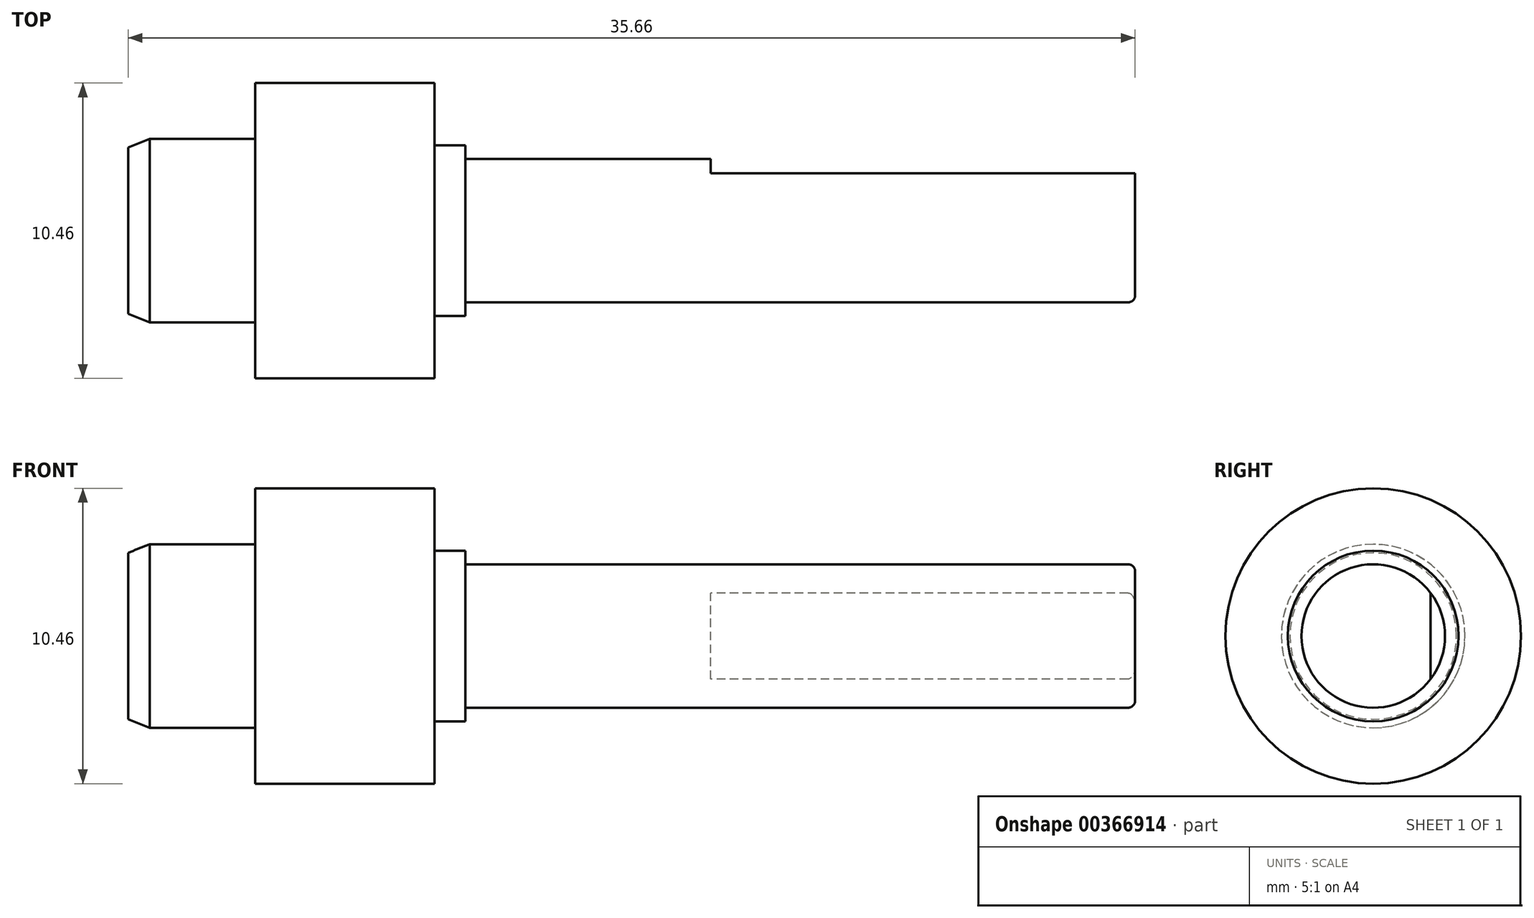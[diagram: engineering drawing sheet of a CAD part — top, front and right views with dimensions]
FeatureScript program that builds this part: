
annotation { "Feature Type Name" : "Feature", "Feature Type Description" : "" }
export const myFeature = defineFeature(function(context is Context, id is Id, definition is map)
    precondition{}
    {
        {
            var Q0;
            Q0=qCreatedBy(makeId("Right.planeOp"),FACE);
            var sketch = newSketch(context, id + "F0", { "sketchPlane" : qUnion([Q0])});
            skCircle(sketch, "E0", {"center": v(0, 0) * mm, "radius": 3.25 * mm});
            skSolve(sketch);
        }
        {
            var Q0;
            Q0 = qSketchRegion(id + "F0", true);
            extrude(context, id + "F1", {"entities" : qUnion([Q0]), "depth" : 4.5 * mm, "offsetDistance" : 25.4 * mm});
        }
        {
            var Q0;
            Q0=makeQuery(id+"F1.opExtrude","CAP_FACE",FACE,{"disambiguationData":[OSD([sQuery(id+"F0.wireOp",EDGE,"E0")])],"isStart":false});
            var sketch = newSketch(context, id + "F2", { "sketchPlane" : qUnion([Q0])});
            skCircle(sketch, "E1", {"center": v(0, 0) * mm, "radius": 5.23 * mm});
            skSolve(sketch);
        }
        {
            var Q0;
            Q0 = qSketchRegion(id + "F2", true);
            extrude(context, id + "F3", {"entities" : qUnion([Q0]), "operationType" : NewBodyOperationType.ADD, "depth" : 6.35 * mm, "offsetDistance" : 25.4 * mm});
        }
        {
            var Q0;
            Q0=makeQuery(id+"F3.opExtrude","CAP_FACE",FACE,{"disambiguationData":[OSD([sQuery(id+"F2.wireOp",EDGE,"E1")])],"isStart":false});
            var sketch = newSketch(context, id + "F4", { "sketchPlane" : qUnion([Q0])});
            skCircle(sketch, "E2", {"center": v(0, 0) * mm, "radius": 3.02 * mm});
            skSolve(sketch);
        }
        {
            var Q0;
            Q0 = qSketchRegion(id + "F4", true);
            extrude(context, id + "F5", {"entities" : qUnion([Q0]), "operationType" : NewBodyOperationType.ADD, "depth" : 1.1 * mm, "offsetDistance" : 25.4 * mm});
        }
        {
            var Q0;
            Q0=makeQuery(id+"F5.opExtrude","CAP_FACE",FACE,{"disambiguationData":[OSD([sQuery(id+"F4.wireOp",EDGE,"E2")])],"isStart":false});
            var sketch = newSketch(context, id + "F6", { "sketchPlane" : qUnion([Q0])});
            skCircle(sketch, "E3", {"center": v(0, 0) * mm, "radius": 2.54 * mm});
            skSolve(sketch);
        }
        {
            var Q0;
            Q0 = qSketchRegion(id + "F6", true);
            extrude(context, id + "F7", {"entities" : qUnion([Q0]), "operationType" : NewBodyOperationType.ADD, "depth" : 23.72 * mm, "offsetDistance" : 25.4 * mm});
        }
        {
            var Q0;
            Q0=qCreatedBy(makeId("Top.planeOp"),FACE);
            cPlane(context, id + "F8", {"entities" : qUnion([Q0]), "cplaneType" : CPlaneType.OFFSET, "offset" : 2.54 * mm, "width" : 152.4 * mm, "height" : 152.4 * mm});
        }
        {
            var Q0;
            Q0=qCreatedBy(id+"F8.planeOp",FACE);
            var sketch = newSketch(context, id + "F9", { "sketchPlane" : qUnion([Q0])});
            skLineSegment(sketch, "E4", {"start": v(0, 0) * mm, "end": v(0, 2.54) * mm});
            skLineSegment(sketch, "E5", {"start": v(0, 2.54) * mm, "end": v(35.66, 2.54) * mm});
            skLineSegment(sketch, "E6", {"start": v(35.66, 2.54) * mm, "end": v(35.66, 2.03) * mm});
            skLineSegment(sketch, "E7", {"start": v(35.66, 2.03) * mm, "end": v(20.62, 2.03) * mm});
            skLineSegment(sketch, "E8", {"start": v(20.62, 2.03) * mm, "end": v(20.62, 2.54) * mm});
            skSolve(sketch);
        }
        {
            var Q0;
            Q0 = qSketchRegion(id + "F9", true);
            extrude(context, id + "F10", {"entities" : qUnion([Q0]), "operationType" : NewBodyOperationType.REMOVE, "endBound" : BoundingType.THROUGH_ALL, "oppositeDirection" : true, "depth" : 25.4 * mm, "offsetDistance" : 25.4 * mm});
        }
        {
            var Q0;
            Q0=makeQuery(id+"F7.opExtrude","CAP_EDGE",EDGE,{"disambiguationData":[OSD([sQuery(id+"F6.wireOp",EDGE,"E3")])],"isStart":false});
            fillet(context, id + "F11", {"entities" : qUnion([Q0]), "radius" : 0.25 * mm, "tangentPropagation" : true, "allowEdgeOverflow" : false});
        }
        {
            var Q0;
            Q0=makeQuery(id+"F1.opExtrude","CAP_FACE",FACE,{"disambiguationData":[OSD([sQuery(id+"F0.wireOp",EDGE,"E0")])],"isStart":true});
            var sketch = newSketch(context, id + "F12", { "sketchPlane" : qUnion([Q0])});
            skCircle(sketch, "E9", {"center": v(0, 0) * mm, "radius": 3.25 * mm});
            skSolve(sketch);
        }
        {
            var Q0;
            Q0 = qSketchRegion(id + "F12", true);
            extrude(context, id + "F13", {"entities" : qUnion([Q0]), "operationType" : NewBodyOperationType.REMOVE, "oppositeDirection" : true, "depth" : 0.76 * mm, "offsetDistance" : 25.4 * mm});
        }
        {
            var Q0;
            Q0=makeQuery(id+"F13.boolean.opBoolean","COPY",FACE,{"derivedFrom":makeQuery(id+"F13.opExtrude","CAP_FACE",FACE,{"disambiguationData":[OSD([sQuery(id+"F12.wireOp",EDGE,"E9")])],"isStart":false})});
            var sketch = newSketch(context, id + "F14", { "sketchPlane" : qUnion([Q0])});
            skCircle(sketch, "E10", {"center": v(0, 0) * mm, "radius": 2.95 * mm});
            skSolve(sketch);
        }
        {
            var Q0;
            Q0 = qSketchRegion(id + "F14", true);
            extrude(context, id + "F15", {"entities" : qUnion([Q0]), "operationType" : NewBodyOperationType.ADD, "depth" : 0.76 * mm, "offsetDistance" : 25.4 * mm});
        }
        {
            var Q0;
            Q0=qCreatedBy(makeId("Front.planeOp"),FACE);
            var sketch = newSketch(context, id + "F16", { "sketchPlane" : qUnion([Q0])});
            skLineSegment(sketch, "E11", {"start": v(0, 0) * mm, "end": v(0.76, 0) * mm});
            skLineSegment(sketch, "E12", {"start": v(0.76, 2.95) * mm, "end": v(0.76, 3.25) * mm});
            skLineSegment(sketch, "E13", {"start": v(0.76, 3.25) * mm, "end": v(0, 2.95) * mm});
            skLineSegment(sketch, "E14", {"start": v(0, 2.95) * mm, "end": v(0.76, 2.95) * mm});
            skSolve(sketch);
        }
        {
            var Q0;
            Q0 = qSketchRegion(id + "F16", true);
            var Q1;
            Q1=sQuery(id+"F16.wireOp",EDGE,"E11");
            revolve(context, id + "F17", {"operationType" : NewBodyOperationType.ADD, "surfaceOperationType" : NewSurfaceOperationType.NEW, "entities" : qUnion([Q0]), "axis" : qUnion([Q1]), "revolveType" : RevolveType.FULL});
        }
    });
